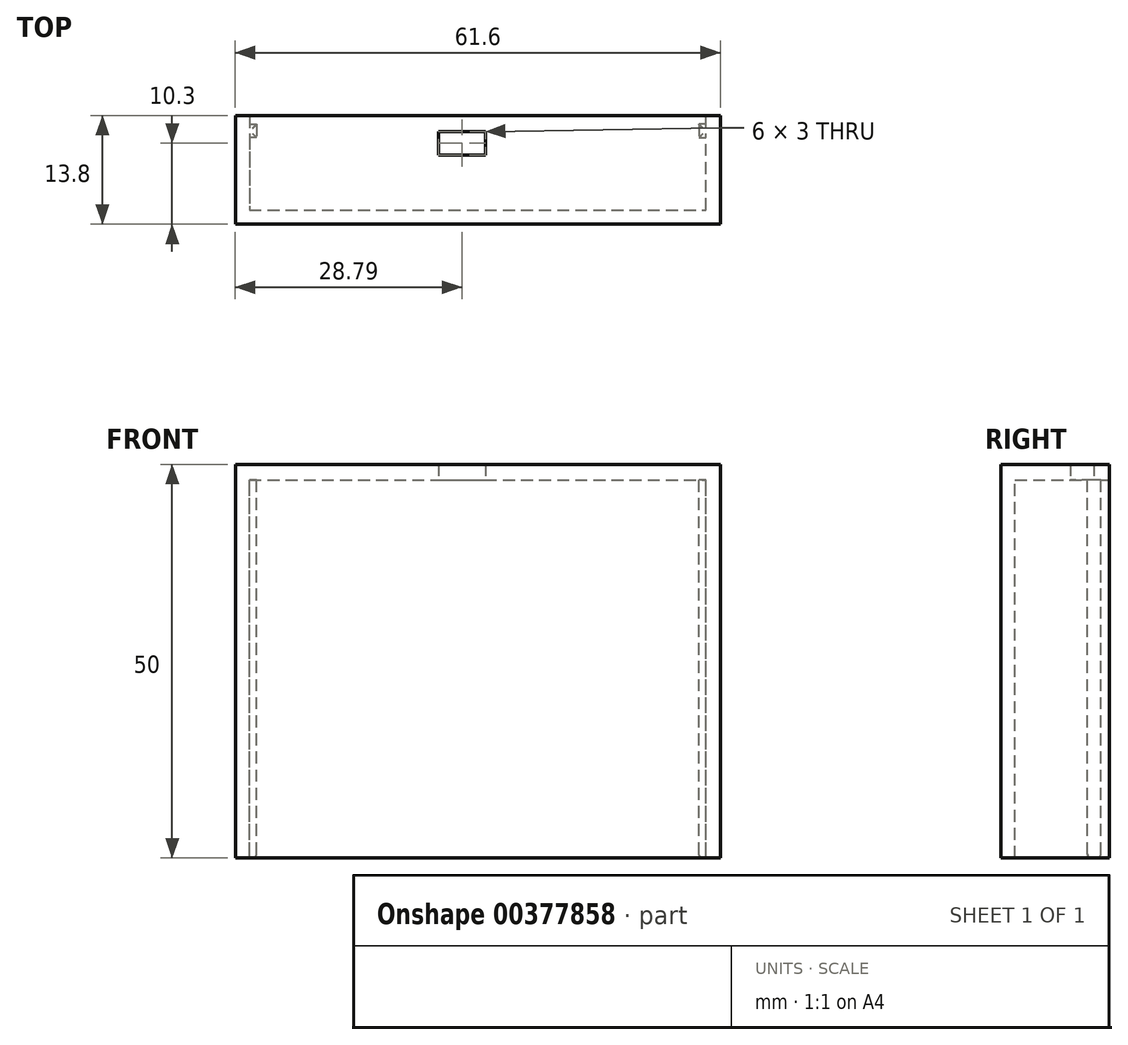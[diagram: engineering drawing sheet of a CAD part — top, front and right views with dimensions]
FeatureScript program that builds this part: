
annotation { "Feature Type Name" : "Feature", "Feature Type Description" : "" }
export const myFeature = defineFeature(function(context is Context, id is Id, definition is map)
    precondition{}
    {
        {
            var Q0;
            Q0=qCreatedBy(makeId("Top.planeOp"),FACE);
            var sketch = newSketch(context, id + "F0", { "sketchPlane" : qUnion([Q0])});
            skLineSegment(sketch, "E0", {"start": v(-28.79, 13.8) * mm, "end": v(-28.79, 0) * mm});
            skLineSegment(sketch, "E1", {"start": v(-28.79, 0) * mm, "end": v(32.81, 0) * mm});
            skLineSegment(sketch, "E2", {"start": v(32.81, 0) * mm, "end": v(32.81, 13.8) * mm});
            skLineSegment(sketch, "E3.0", {"start": v(31.01, 1.8) * mm, "end": v(31.01, 13.8) * mm});
            skLineSegment(sketch, "E3.1", {"start": v(-26.99, 1.8) * mm, "end": v(31.01, 1.8) * mm});
            skLineSegment(sketch, "E3.2", {"start": v(-26.99, 13.8) * mm, "end": v(-26.99, 1.8) * mm});
            skLineSegment(sketch, "E4", {"start": v(-28.79, 13.8) * mm, "end": v(-26.99, 13.8) * mm});
            skLineSegment(sketch, "E5", {"start": v(32.81, 13.8) * mm, "end": v(31.01, 13.8) * mm});
            skLineSegment(sketch, "E6", {"start": v(-26.99, 13.8) * mm, "end": v(31.01, 13.8) * mm});
            skLineSegment(sketch, "E7.bottom", {"start": v(-3, 11.8) * mm, "end": v(3, 11.8) * mm});
            skLineSegment(sketch, "E7.top", {"start": v(-3, 8.8) * mm, "end": v(3, 8.8) * mm});
            skLineSegment(sketch, "E7.left", {"start": v(-3, 11.8) * mm, "end": v(-3, 8.8) * mm});
            skLineSegment(sketch, "E7.right", {"start": v(3, 11.8) * mm, "end": v(3, 8.8) * mm});
            skLineSegment(sketch, "E8", {"start": v(-26.99, 12.7) * mm, "end": v(-26.09, 12.7) * mm});
            skLineSegment(sketch, "E9", {"start": v(-26.09, 12.7) * mm, "end": v(-26.09, 11) * mm});
            skLineSegment(sketch, "E10", {"start": v(-26.09, 11) * mm, "end": v(-26.99, 11) * mm});
            skLineSegment(sketch, "E11", {"start": v(31.01, 12.7) * mm, "end": v(30.11, 12.7) * mm});
            skLineSegment(sketch, "E12", {"start": v(30.11, 12.7) * mm, "end": v(30.11, 11) * mm});
            skLineSegment(sketch, "E13", {"start": v(30.11, 11) * mm, "end": v(31.01, 11) * mm});
            skSolve(sketch);
        }
        {
            var Q0;
            Q0=makeQuery(id+"F0.imprint","IMPRINT",FACE,{"disambiguationData":[TD([[makeQuery(id+"F0.imprint","IMPRINT",EDGE,{"derivedFrom":sQuery(id+"F0.wireOp",EDGE,"E0")}),1.0]])]});
            var Q1;
            {var subQ0=sQuery(id+"F0.wireOp",EDGE,"E8");Q1=makeQuery(id+"F0.imprint","IMPRINT",FACE,{"disambiguationData":[TD([[makeQuery(id+"F0.imprint","IMPRINT",EDGE,{"derivedFrom":subQ0}),-1.0]])]});}
            var Q2;
            {var subQ0=sQuery(id+"F0.wireOp",EDGE,"E11");Q2=makeQuery(id+"F0.imprint","IMPRINT",FACE,{"disambiguationData":[TD([[makeQuery(id+"F0.imprint","IMPRINT",EDGE,{"derivedFrom":subQ0}),1.0]])]});}
            extrude(context, id + "F1", {"entities" : qUnion([Q0, Q1, Q2]), "oppositeDirection" : true, "depth" : 48 * mm});
        }
        {
            var Q0;
            {var subQ2=sQuery(id+"F0.wireOp",EDGE,"E3.1");Q0=makeQuery(id+"F0.imprint","IMPRINT",FACE,{"disambiguationData":[TD([[makeQuery(id+"F0.imprint","IMPRINT",EDGE,{"derivedFrom":subQ2}),1.0]])]});}
            var Q1;
            Q1=makeQuery(id+"F0.imprint","IMPRINT",FACE,{"disambiguationData":[TD([[makeQuery(id+"F0.imprint","IMPRINT",EDGE,{"derivedFrom":sQuery(id+"F0.wireOp",EDGE,"E0")}),1.0]])]});
            var Q2;
            {var subQ0=sQuery(id+"F0.wireOp",EDGE,"E8");Q2=makeQuery(id+"F0.imprint","IMPRINT",FACE,{"disambiguationData":[TD([[makeQuery(id+"F0.imprint","IMPRINT",EDGE,{"derivedFrom":subQ0}),-1.0]])]});}
            var Q3;
            {var subQ0=sQuery(id+"F0.wireOp",EDGE,"E11");Q3=makeQuery(id+"F0.imprint","IMPRINT",FACE,{"disambiguationData":[TD([[makeQuery(id+"F0.imprint","IMPRINT",EDGE,{"derivedFrom":subQ0}),1.0]])]});}
            extrude(context, id + "F2", {"entities" : qUnion([Q0, Q1, Q2, Q3]), "operationType" : NewBodyOperationType.ADD, "depth" : 2 * mm});
        }
        {
            var Q0;
            Q0=makeQuery(id+"F1.opExtrude","CAP_EDGE",EDGE,{"disambiguationData":[OSD([sQuery(id+"F0.wireOp",EDGE,"E10")])],"isStart":false});
            var Q1;
            Q1=makeQuery(id+"F1.opExtrude","CAP_EDGE",EDGE,{"disambiguationData":[OSD([sQuery(id+"F0.wireOp",EDGE,"E8")])],"isStart":false});
            var Q2;
            Q2=makeQuery(id+"F1.opExtrude","CAP_EDGE",EDGE,{"disambiguationData":[OSD([sQuery(id+"F0.wireOp",EDGE,"E9")])],"isStart":false});
            var Q3;
            Q3=makeQuery(id+"F1.opExtrude","CAP_EDGE",EDGE,{"disambiguationData":[OSD([sQuery(id+"F0.wireOp",EDGE,"E13")])],"isStart":false});
            var Q4;
            Q4=makeQuery(id+"F1.opExtrude","CAP_EDGE",EDGE,{"disambiguationData":[OSD([sQuery(id+"F0.wireOp",EDGE,"E11")])],"isStart":false});
            var Q5;
            Q5=makeQuery(id+"F1.opExtrude","CAP_EDGE",EDGE,{"disambiguationData":[OSD([sQuery(id+"F0.wireOp",EDGE,"E12")])],"isStart":false});
            fillet(context, id + "F3", {"entities" : qUnion([Q0, Q1, Q2, Q3, Q4, Q5]), "radius" : 0.5 * mm, "tangentPropagation" : true, "allowEdgeOverflow" : false});
        }
    });
